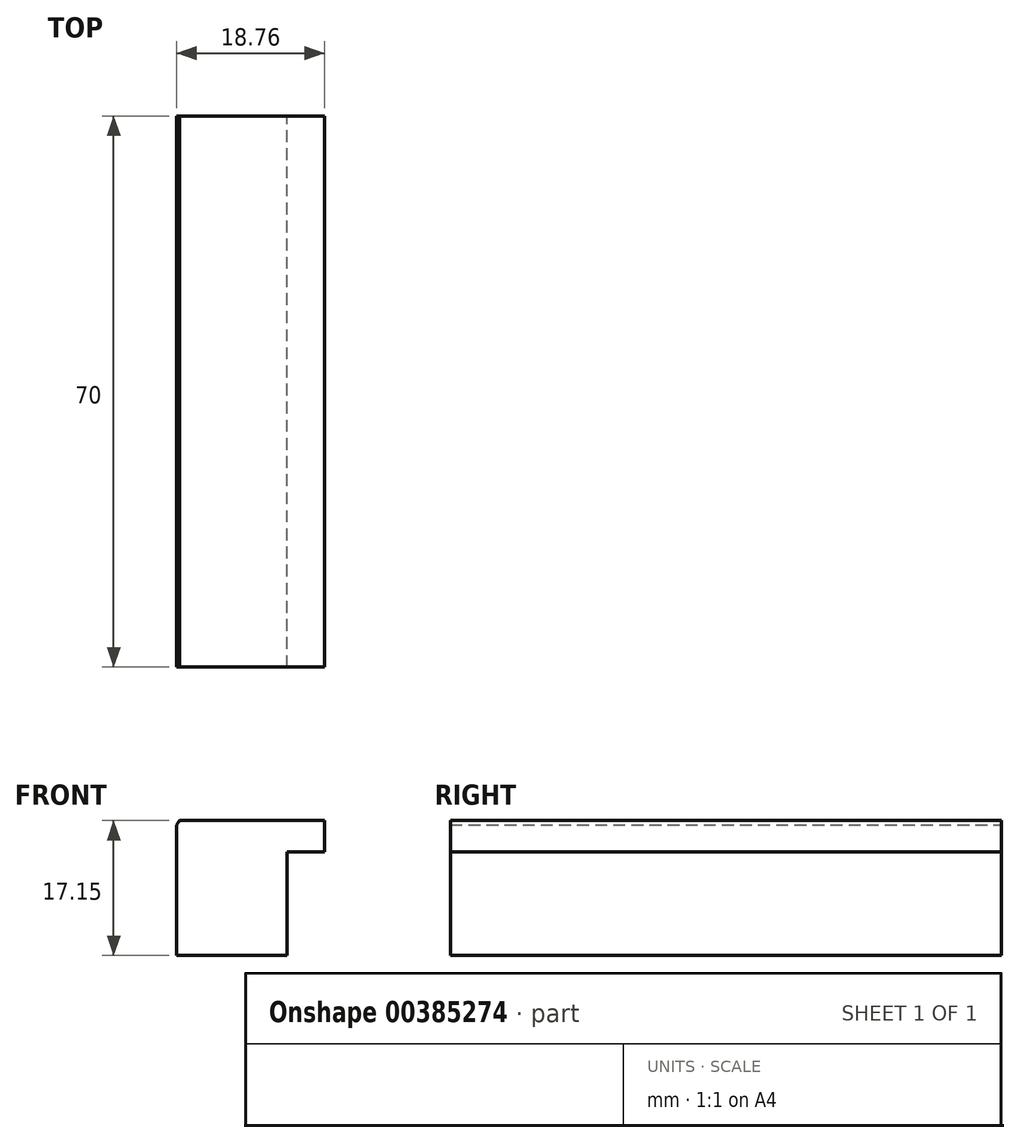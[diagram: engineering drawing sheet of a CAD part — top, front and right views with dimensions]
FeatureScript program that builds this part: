
annotation { "Feature Type Name" : "Feature", "Feature Type Description" : "" }
export const myFeature = defineFeature(function(context is Context, id is Id, definition is map)
    precondition{}
    {
        {
            var Q0;
            Q0=qCreatedBy(makeId("Front.planeOp"),FACE);
            var sketch = newSketch(context, id + "F0", { "sketchPlane" : qUnion([Q0])});
            skLineSegment(sketch, "E0", {"start": v(-42.04, -3.91) * mm, "end": v(-28.05, -3.91) * mm});
            skLineSegment(sketch, "E1", {"start": v(-28.05, -3.91) * mm, "end": v(-28.05, 9.24) * mm});
            skLineSegment(sketch, "E2", {"start": v(-23.28, 13.24) * mm, "end": v(-41.67, 13.24) * mm});
            skLineSegment(sketch, "E3", {"start": v(-42.04, 12.67) * mm, "end": v(-42.04, -3.91) * mm});
            skLineSegment(sketch, "E4", {"start": v(-23.28, 9.24) * mm, "end": v(-28.05, 9.24) * mm});
            skLineSegment(sketch, "E5", {"start": v(-23.28, 13.24) * mm, "end": v(-23.28, 9.24) * mm});
            skPoint(sketch, "E6.orphan", {"position": v(-20.05, 13.24) * mm});
            skLineSegment(sketch, "E7", {"start": v(-41.67, 13.24) * mm, "end": v(-42.04, 12.67) * mm});
            skPoint(sketch, "E8.orphan", {"position": v(-42.04, 13.24) * mm});
            skSolve(sketch);
        }
        {
            var Q0;
            Q0=makeQuery(id+"F0.imprint","IMPRINT",FACE,{"disambiguationData":[TD([[makeQuery(id+"F0.imprint","IMPRINT",EDGE,{"derivedFrom":sQuery(id+"F0.wireOp",EDGE,"E0")}),1.0]])]});
            extrude(context, id + "F1", {"entities" : qUnion([Q0]), "depth" : 70 * mm});
        }
    });
